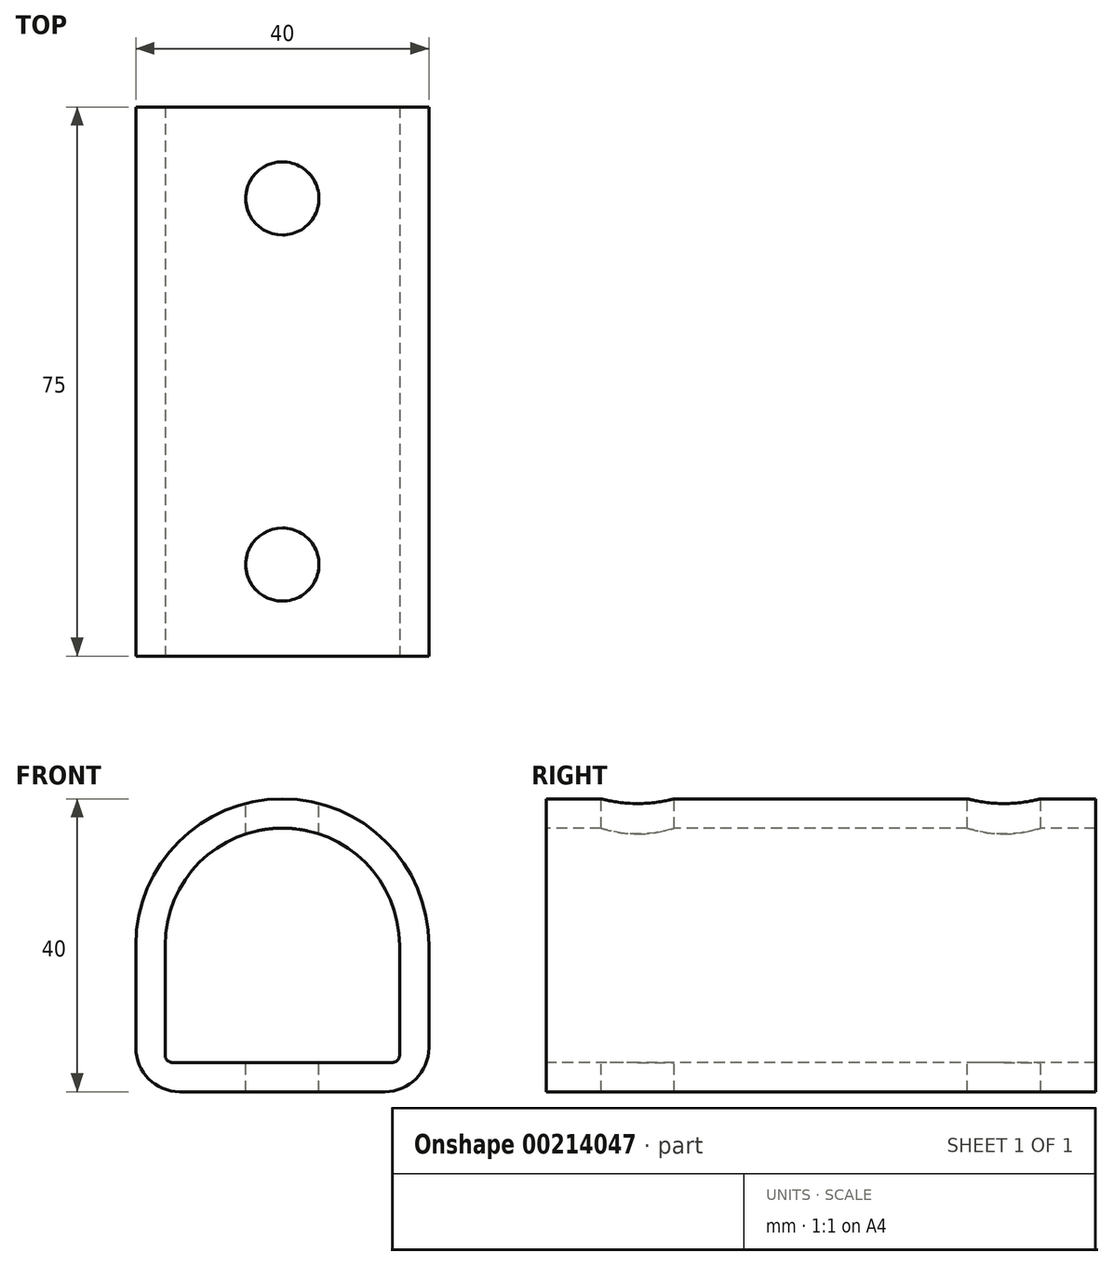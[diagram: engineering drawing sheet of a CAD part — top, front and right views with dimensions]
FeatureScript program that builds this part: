
annotation { "Feature Type Name" : "Feature", "Feature Type Description" : "" }
export const myFeature = defineFeature(function(context is Context, id is Id, definition is map)
    precondition{}
    {
        {
            var Q0;
            Q0=qCreatedBy(makeId("Top.planeOp"),FACE);
            var sketch = newSketch(context, id + "F0", { "sketchPlane" : qUnion([Q0])});
            skLineSegment(sketch, "E0.bottom", {"start": v(20, 37.5) * mm, "end": v(-20, 37.5) * mm});
            skLineSegment(sketch, "E0.top", {"start": v(20, -37.5) * mm, "end": v(-20, -37.5) * mm});
            skLineSegment(sketch, "E0.left", {"start": v(20, 37.5) * mm, "end": v(20, -37.5) * mm});
            skLineSegment(sketch, "E0.right", {"start": v(-20, 37.5) * mm, "end": v(-20, -37.5) * mm});
            skPoint(sketch, "E0.middle", {"position": v(0, 0) * mm});
            skSolve(sketch);
        }
        {
            var Q0;
            Q0=makeQuery(id+"F0.imprint","IMPRINT",FACE,{"disambiguationData":[TD([[makeQuery(id+"F0.imprint","IMPRINT",EDGE,{"derivedFrom":sQuery(id+"F0.wireOp",EDGE,"E0.bottom")}),1.0]])]});
            extrude(context, id + "F1", {"entities" : qUnion([Q0]), "depth" : 40 * mm});
        }
        {
            var Q0;
            Q0=makeQuery(id+"F1.opExtrude","CAP_FACE",FACE,{"disambiguationData":[OSD([sQuery(id+"F0.wireOp",EDGE,"E0.bottom"),sQuery(id+"F0.wireOp",EDGE,"E0.top"),sQuery(id+"F0.wireOp",EDGE,"E0.left"),sQuery(id+"F0.wireOp",EDGE,"E0.right")])],"isStart":false});
            var sketch = newSketch(context, id + "F2", { "sketchPlane" : qUnion([Q0])});
            skPoint(sketch, "E1", {"position": v(0, 25) * mm});
            skPoint(sketch, "E2", {"position": v(0, -25) * mm});
            skSolve(sketch);
        }
        {
            var Q0;
            Q0=sQuery(id+"F2.wireOp",VERTEX,"E1");
            var Q1;
            Q1=sQuery(id+"F2.wireOp",VERTEX,"E2");
            var Q2;
            Q2=makeQuery(id+"F1.opExtrude","SWEPT_BODY",BODY,{"disambiguationData":[OSD([sQuery(id+"F0.wireOp",EDGE,"E0.bottom"),sQuery(id+"F0.wireOp",EDGE,"E0.top"),sQuery(id+"F0.wireOp",EDGE,"E0.left"),sQuery(id+"F0.wireOp",EDGE,"E0.right")])]});
            hole(context, id + "F3", {"style" : HoleStyle.SIMPLE, "endStyle" : HoleEndStyle.THROUGH, "standardTappedOrClearance" : lookupTablePath({ "standard" : "ISO", "size" : "10", "type" : "Drilled" }), "standardBlindInLast" : lookupTablePath({ "standard" : "ISO", "size" : "10", "type" : "Drilled" }), "holeDiameter" : 10 * mm, "locations" : qUnion([Q0, Q1]), "scope" : qUnion([Q2]), "isTappedThrough" : true});
        }
        {
            var Q0;
            Q0=makeQuery(id+"F1.opExtrude","CAP_EDGE",EDGE,{"disambiguationData":[OSD([sQuery(id+"F0.wireOp",EDGE,"E0.left")])],"isStart":false});
            fillet(context, id + "F4", {"entities" : qUnion([Q0]), "radius" : 20 * mm, "tangentPropagation" : true, "allowEdgeOverflow" : false});
        }
        {
            var Q0;
            Q0=makeQuery(id+"F1.opExtrude","CAP_EDGE",EDGE,{"disambiguationData":[OSD([sQuery(id+"F0.wireOp",EDGE,"E0.right")])],"isStart":false});
            fillet(context, id + "F5", {"entities" : qUnion([Q0]), "radius" : 20 * mm, "tangentPropagation" : true, "allowEdgeOverflow" : false});
        }
        {
            var Q0;
            Q0=makeQuery(id+"F1.opExtrude","CAP_EDGE",EDGE,{"disambiguationData":[OSD([sQuery(id+"F0.wireOp",EDGE,"E0.right")])],"isStart":true});
            var Q1;
            Q1=makeQuery(id+"F1.opExtrude","CAP_EDGE",EDGE,{"disambiguationData":[OSD([sQuery(id+"F0.wireOp",EDGE,"E0.left")])],"isStart":true});
            fillet(context, id + "F6", {"entities" : qUnion([Q0, Q1]), "radius" : 6 * mm, "tangentPropagation" : true, "allowEdgeOverflow" : false});
        }
        {
            var Q0;
            Q0=makeQuery(id+"F1.opExtrude","SWEPT_FACE",FACE,{"disambiguationData":[OSD([sQuery(id+"F0.wireOp",EDGE,"E0.top")])]});
            var sketch = newSketch(context, id + "F7", { "sketchPlane" : qUnion([Q0])});
            skPoint(sketch, "E3.endSnap0", {"position": v(0, 0) * mm});
            skLineSegment(sketch, "E4", {"start": v(-16, 4) * mm, "end": v(-16, 20) * mm});
            skArc(sketch, "E5", {"start": v(-16, 20) * mm, "mid": v(0, 36) * mm, "end": v(16, 20) * mm});
            skLineSegment(sketch, "E6", {"start": v(16, 20) * mm, "end": v(16, 4) * mm});
            skLineSegment(sketch, "E7", {"start": v(-16, 4) * mm, "end": v(16, 4) * mm});
            skSolve(sketch);
        }
        {
            var Q0;
            Q0=makeQuery(id+"F7.imprint","IMPRINT",FACE,{"disambiguationData":[TD([[makeQuery(id+"F7.imprint","IMPRINT",EDGE,{"derivedFrom":sQuery(id+"F7.wireOp",EDGE,"E4")}),-1.0]])]});
            extrude(context, id + "F8", {"entities" : qUnion([Q0]), "operationType" : NewBodyOperationType.REMOVE, "endBound" : BoundingType.THROUGH_ALL, "oppositeDirection" : true, "depth" : 75 * mm});
        }
        {
            var Q0;
            Q0=makeQuery(id+"F8.boolean.opBoolean","COPY",EDGE,{"derivedFrom":makeQuery(id+"F8.opExtrude","SWEPT_EDGE",EDGE,{"disambiguationData":[OSD([sQuery(id+"F7.wireOp",EDGE,"E4"),sQuery(id+"F7.wireOp",EDGE,"E7")])]})});
            var Q1;
            Q1=makeQuery(id+"F8.boolean.opBoolean","COPY",EDGE,{"derivedFrom":makeQuery(id+"F8.opExtrude","SWEPT_EDGE",EDGE,{"disambiguationData":[OSD([sQuery(id+"F7.wireOp",EDGE,"E6"),sQuery(id+"F7.wireOp",EDGE,"E7")])]})});
            fillet(context, id + "F9", {"entities" : qUnion([Q0, Q1]), "radius" : 1 * mm, "tangentPropagation" : true, "allowEdgeOverflow" : false});
        }
    });
